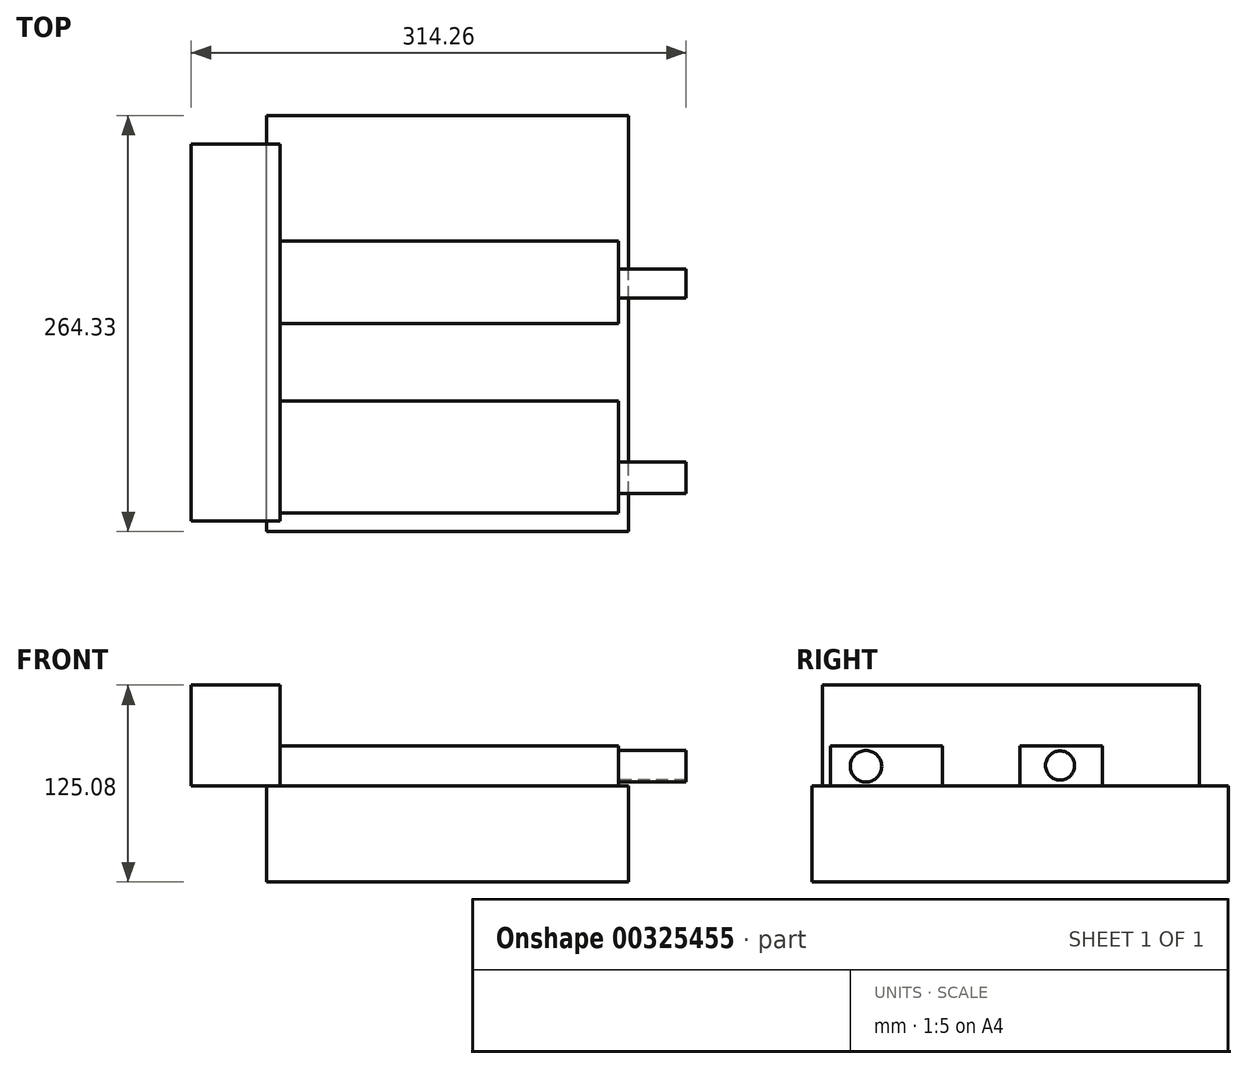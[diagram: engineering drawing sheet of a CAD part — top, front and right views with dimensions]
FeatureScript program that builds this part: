
annotation { "Feature Type Name" : "Feature", "Feature Type Description" : "" }
export const myFeature = defineFeature(function(context is Context, id is Id, definition is map)
    precondition{}
    {
        {
            var Q0;
            Q0=qCreatedBy(makeId("Right.planeOp"),FACE);
            var sketch = newSketch(context, id + "F0", { "sketchPlane" : qUnion([Q0])});
            skLineSegment(sketch, "E0.bottom", {"start": v(-55.2, -23.58) * mm, "end": v(209.13, -23.58) * mm});
            skLineSegment(sketch, "E0.top", {"start": v(-55.2, -84.65) * mm, "end": v(209.13, -84.65) * mm});
            skLineSegment(sketch, "E0.left", {"start": v(-55.2, -23.58) * mm, "end": v(-55.2, -84.65) * mm});
            skLineSegment(sketch, "E0.right", {"start": v(209.13, -23.58) * mm, "end": v(209.13, -84.65) * mm});
            skSolve(sketch);
        }
        {
            var Q0;
            Q0 = qSketchRegion(id + "F0", true);
            extrude(context, id + "F1", {"entities" : qUnion([Q0]), "oppositeDirection" : true, "depth" : 229.87 * mm});
        }
        {
            var Q0;
            Q0=makeQuery(id+"F1.opExtrude","SWEPT_FACE",FACE,{"disambiguationData":[OSD([sQuery(id+"F0.wireOp",EDGE,"E0.bottom")])]});
            var sketch = newSketch(context, id + "F2", { "sketchPlane" : qUnion([Q0])});
            skLineSegment(sketch, "E1.bottom", {"start": v(-221.53, 190.83) * mm, "end": v(-277.8, 190.83) * mm});
            skLineSegment(sketch, "E1.top", {"start": v(-221.53, -48.47) * mm, "end": v(-277.8, -48.47) * mm});
            skLineSegment(sketch, "E1.left", {"start": v(-221.53, 190.83) * mm, "end": v(-221.53, -48.47) * mm});
            skLineSegment(sketch, "E1.right", {"start": v(-277.8, 190.83) * mm, "end": v(-277.8, -48.47) * mm});
            skSolve(sketch);
        }
        {
            var Q0;
            Q0 = qSketchRegion(id + "F2", true);
            extrude(context, id + "F3", {"entities" : qUnion([Q0]), "operationType" : NewBodyOperationType.ADD, "depth" : 64 * mm});
        }
        {
            var Q0;
            Q0=makeQuery(id+"F1.opExtrude","SWEPT_FACE",FACE,{"disambiguationData":[OSD([sQuery(id+"F0.wireOp",EDGE,"E0.bottom")])]});
            var sketch = newSketch(context, id + "F4", { "sketchPlane" : qUnion([Q0])});
            skLineSegment(sketch, "E2.bottom", {"start": v(-221.53, 27.63) * mm, "end": v(-6.47, 27.63) * mm});
            skLineSegment(sketch, "E2.top", {"start": v(-221.53, -43.5) * mm, "end": v(-6.47, -43.5) * mm});
            skLineSegment(sketch, "E2.left", {"start": v(-221.53, 27.63) * mm, "end": v(-221.53, -43.5) * mm});
            skLineSegment(sketch, "E2.right", {"start": v(-6.47, 27.63) * mm, "end": v(-6.47, -43.5) * mm});
            skPoint(sketch, "E3.oppositeSnap0", {"position": v(0, 76.96) * mm});
            skLineSegment(sketch, "E3.bottom", {"start": v(-221.53, 129.3) * mm, "end": v(-6.47, 129.3) * mm});
            skLineSegment(sketch, "E3.top", {"start": v(-221.53, 76.96) * mm, "end": v(-6.47, 76.96) * mm});
            skLineSegment(sketch, "E3.left", {"start": v(-221.53, 129.3) * mm, "end": v(-221.53, 76.96) * mm});
            skLineSegment(sketch, "E3.right", {"start": v(-6.47, 129.3) * mm, "end": v(-6.47, 76.96) * mm});
            skSolve(sketch);
        }
        {
            var Q0;
            Q0 = qSketchRegion(id + "F4", true);
            extrude(context, id + "F5", {"entities" : qUnion([Q0]), "operationType" : NewBodyOperationType.ADD, "depth" : 25.4 * mm});
        }
        {
            var Q0;
            Q0=makeQuery(id+"F5.opExtrude","SWEPT_FACE",FACE,{"disambiguationData":[OSD([sQuery(id+"F4.wireOp",EDGE,"E2.right")])]});
            var sketch = newSketch(context, id + "F6", { "sketchPlane" : qUnion([Q0])});
            skCircle(sketch, "E4", {"center": v(-20.92, -11.13) * mm, "radius": 10.02 * mm});
            skCircle(sketch, "E5", {"center": v(102.37, -10.65) * mm, "radius": 9.22 * mm});
            skSolve(sketch);
        }
        {
            var Q0;
            Q0 = qSketchRegion(id + "F6", true);
            extrude(context, id + "F7", {"entities" : qUnion([Q0]), "operationType" : NewBodyOperationType.ADD, "depth" : 42.93 * mm});
        }
    });
